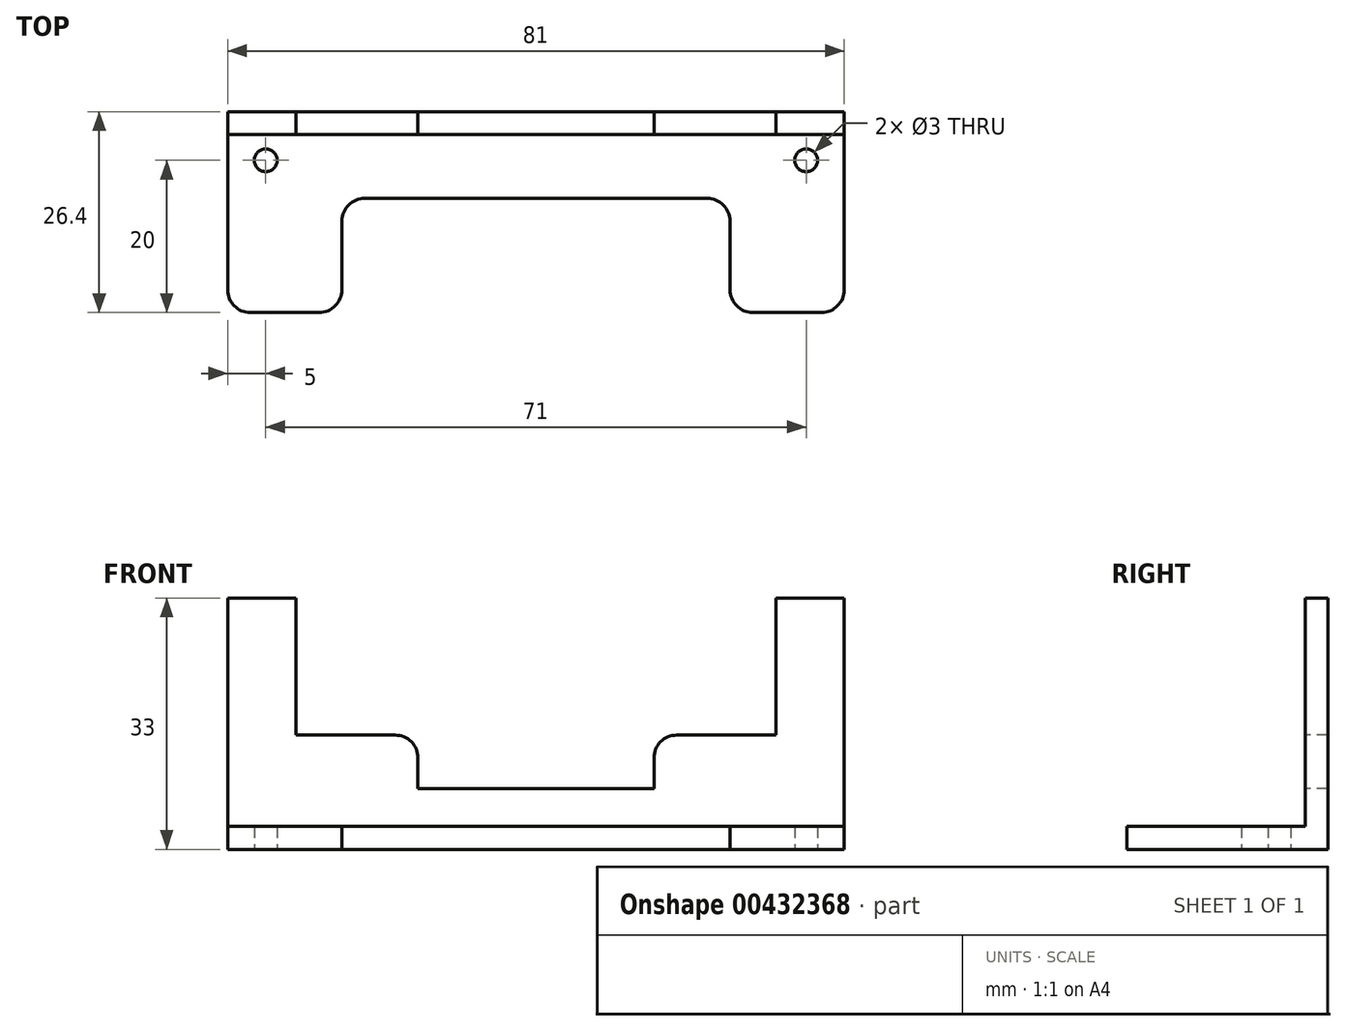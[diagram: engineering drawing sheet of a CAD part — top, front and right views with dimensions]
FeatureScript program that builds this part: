
annotation { "Feature Type Name" : "Feature", "Feature Type Description" : "" }
export const myFeature = defineFeature(function(context is Context, id is Id, definition is map)
    precondition{}
    {
        {
            var Q0;
            Q0=qCreatedBy(makeId("Top.planeOp"),FACE);
            var sketch = newSketch(context, id + "F0", { "sketchPlane" : qUnion([Q0])});
            skLineSegment(sketch, "E0.bottom", {"start": v(0, 11.4) * mm, "end": v(81, 11.4) * mm});
            skLineSegment(sketch, "E0.top", {"start": v(18, 0) * mm, "end": v(63, 0) * mm});
            skLineSegment(sketch, "E0.left", {"start": v(0, 11.4) * mm, "end": v(0, 0) * mm});
            skLineSegment(sketch, "E0.right", {"start": v(81, 11.4) * mm, "end": v(81, 0) * mm});
            skCircle(sketch, "E1", {"center": v(5, 5) * mm, "radius": 1.5 * mm});
            skCircle(sketch, "E2", {"center": v(76, 5) * mm, "radius": 1.5 * mm});
            skLineSegment(sketch, "E3.top", {"start": v(3, -15) * mm, "end": v(12, -15) * mm});
            skLineSegment(sketch, "E3.left", {"start": v(0, 0) * mm, "end": v(0, -12) * mm});
            skLineSegment(sketch, "E3.right", {"start": v(15, -3) * mm, "end": v(15, -12) * mm});
            skLineSegment(sketch, "E4.top", {"start": v(78, -15) * mm, "end": v(69, -15) * mm});
            skLineSegment(sketch, "E4.left", {"start": v(81, 0) * mm, "end": v(81, -12) * mm});
            skLineSegment(sketch, "E4.right", {"start": v(66, -3) * mm, "end": v(66, -12) * mm});
            skPoint(sketch, "E5.visualSharp", {"position": v(15, 0) * mm});
            skArc(sketch, "E5.filletArc", {"start": v(18, 0) * mm, "mid": v(15.88, -0.88) * mm, "end": v(15, -3) * mm});
            skPoint(sketch, "E6.visualSharp", {"position": v(66, 0) * mm});
            skArc(sketch, "E6.filletArc", {"start": v(66, -3) * mm, "mid": v(65.12, -0.88) * mm, "end": v(63, 0) * mm});
            skPoint(sketch, "E7.visualSharp", {"position": v(15, -15) * mm});
            skArc(sketch, "E7.filletArc", {"start": v(12, -15) * mm, "mid": v(14.12, -14.12) * mm, "end": v(15, -12) * mm});
            skPoint(sketch, "E8.visualSharp", {"position": v(0, -15) * mm});
            skArc(sketch, "E8.filletArc", {"start": v(0, -12) * mm, "mid": v(0.88, -14.12) * mm, "end": v(3, -15) * mm});
            skPoint(sketch, "E9.visualSharp", {"position": v(66, -15) * mm});
            skArc(sketch, "E9.filletArc", {"start": v(66, -12) * mm, "mid": v(66.88, -14.12) * mm, "end": v(69, -15) * mm});
            skPoint(sketch, "E10.visualSharp", {"position": v(81, -15) * mm});
            skArc(sketch, "E10.filletArc", {"start": v(78, -15) * mm, "mid": v(80.12, -14.12) * mm, "end": v(81, -12) * mm});
            skSolve(sketch);
        }
        {
            var Q0;
            Q0=makeQuery(id+"F0.imprint","IMPRINT",FACE,{"disambiguationData":[TD([[makeQuery(id+"F0.imprint","IMPRINT",EDGE,{"derivedFrom":sQuery(id+"F0.wireOp",EDGE,"E0.bottom")}),-1.0]])]});
            extrude(context, id + "F1", {"entities" : qUnion([Q0]), "depth" : 3 * mm});
        }
        {
            var Q0;
            Q0=makeQuery(id+"F1.opExtrude","CAP_FACE",FACE,{"disambiguationData":[OSD([sQuery(id+"F0.wireOp",EDGE,"E0.bottom"),sQuery(id+"F0.wireOp",EDGE,"E0.top"),sQuery(id+"F0.wireOp",EDGE,"E0.left"),sQuery(id+"F0.wireOp",EDGE,"E0.right"),sQuery(id+"F0.wireOp",EDGE,"E1"),sQuery(id+"F0.wireOp",EDGE,"E2")])],"isStart":false});
            var sketch = newSketch(context, id + "F2", { "sketchPlane" : qUnion([Q0])});
            skLineSegment(sketch, "E11.bottom", {"start": v(0, 11.4) * mm, "end": v(81, 11.4) * mm});
            skLineSegment(sketch, "E11.top", {"start": v(0, 8.4) * mm, "end": v(81, 8.4) * mm});
            skLineSegment(sketch, "E11.left", {"start": v(0, 11.4) * mm, "end": v(0, 8.4) * mm});
            skLineSegment(sketch, "E11.right", {"start": v(81, 11.4) * mm, "end": v(81, 8.4) * mm});
            skSolve(sketch);
        }
        {
            var Q0;
            Q0 = qSketchRegion(id + "F2", true);
            extrude(context, id + "F3", {"entities" : qUnion([Q0]), "operationType" : NewBodyOperationType.ADD, "depth" : 30 * mm});
        }
        {
            var Q0;
            Q0=makeQuery(id+"F3.opExtrude","SWEPT_FACE",FACE,{"disambiguationData":[OSD([sQuery(id+"F2.wireOp",EDGE,"E11.top")])]});
            var sketch = newSketch(context, id + "F4", { "sketchPlane" : qUnion([Q0])});
            skLineSegment(sketch, "E12.bottom", {"start": v(9, 33) * mm, "end": v(72, 33) * mm});
            skLineSegment(sketch, "E12.top", {"start": v(9, 15) * mm, "end": v(22, 15) * mm});
            skLineSegment(sketch, "E12.left", {"start": v(9, 33) * mm, "end": v(9, 15) * mm});
            skLineSegment(sketch, "E12.right", {"start": v(72, 33) * mm, "end": v(72, 15) * mm});
            skPoint(sketch, "E13.center.orphan", {"position": v(2.93, 24.66) * mm});
            skPoint(sketch, "E14.center.orphan", {"position": v(2.93, 11) * mm});
            skPoint(sketch, "E15.center.orphan", {"position": v(12.93, 11) * mm});
            skPoint(sketch, "E16.center.orphan", {"position": v(64.43, 11) * mm});
            skLineSegment(sketch, "E17.top", {"start": v(25, 8) * mm, "end": v(56, 8) * mm});
            skLineSegment(sketch, "E17.left", {"start": v(25, 12) * mm, "end": v(25, 8) * mm});
            skLineSegment(sketch, "E17.right", {"start": v(56, 12) * mm, "end": v(56, 8) * mm});
            skLineSegment(sketch, "E18.trimOffspring", {"start": v(59, 15) * mm, "end": v(72, 15) * mm});
            skPoint(sketch, "E19.visualSharp", {"position": v(25, 15) * mm});
            skArc(sketch, "E19.filletArc", {"start": v(25, 12) * mm, "mid": v(24.12, 14.12) * mm, "end": v(22, 15) * mm});
            skPoint(sketch, "E20.visualSharp", {"position": v(56, 15) * mm});
            skArc(sketch, "E20.filletArc", {"start": v(59, 15) * mm, "mid": v(56.88, 14.12) * mm, "end": v(56, 12) * mm});
            skSolve(sketch);
        }
        {
            var Q0;
            Q0 = qSketchRegion(id + "F4", true);
            extrude(context, id + "F5", {"entities" : qUnion([Q0]), "operationType" : NewBodyOperationType.REMOVE, "endBound" : BoundingType.UP_TO_NEXT, "oppositeDirection" : true, "depth" : 25 * mm});
        }
    });
